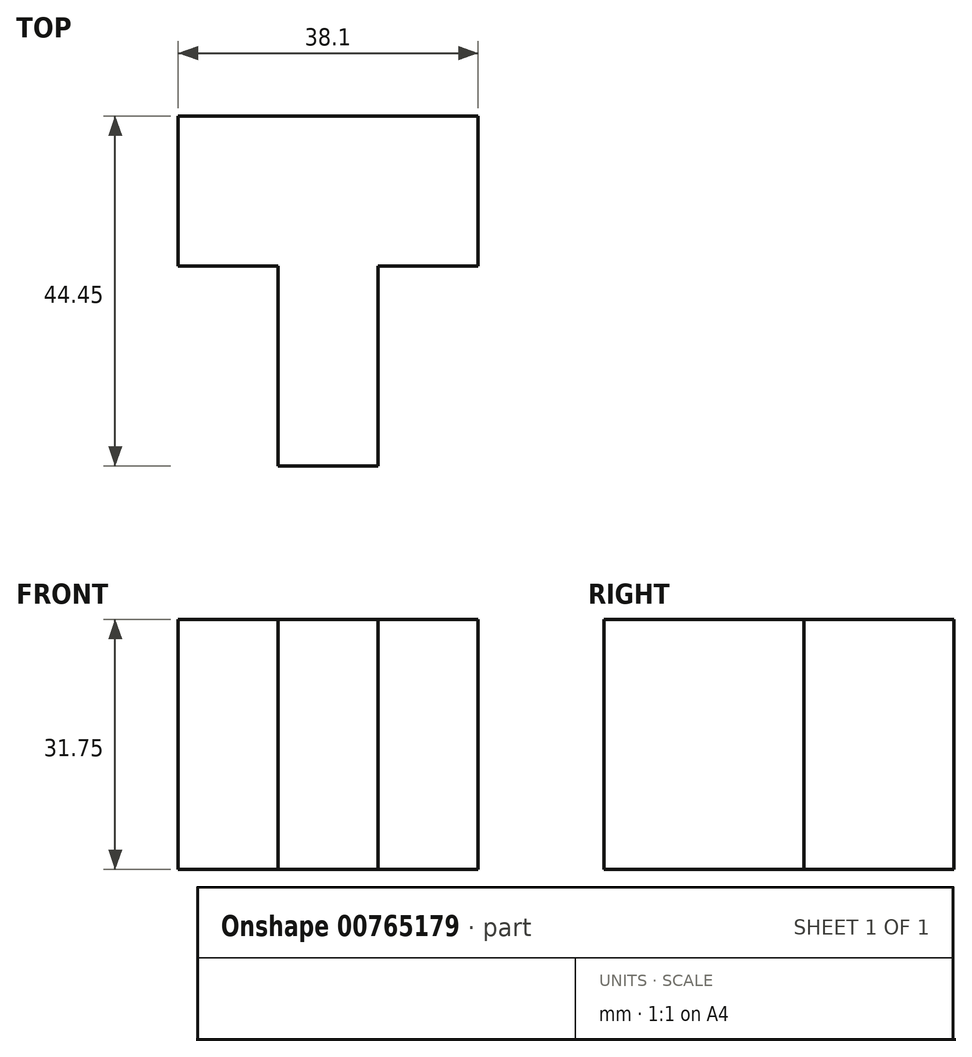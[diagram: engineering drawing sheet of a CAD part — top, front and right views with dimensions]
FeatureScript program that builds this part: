
annotation { "Feature Type Name" : "Feature", "Feature Type Description" : "" }
export const myFeature = defineFeature(function(context is Context, id is Id, definition is map)
    precondition{}
    {
        {
            var Q0;
            Q0=qCreatedBy(makeId("Top.planeOp"),FACE);
            var sketch = newSketch(context, id + "F0", { "sketchPlane" : qUnion([Q0])});
            skLineSegment(sketch, "E0", {"start": v(-25.4, 39.9) * mm, "end": v(12.7, 39.9) * mm});
            skLineSegment(sketch, "E1", {"start": v(-25.4, 39.9) * mm, "end": v(-25.4, 20.85) * mm});
            skLineSegment(sketch, "E2", {"start": v(12.7, 39.9) * mm, "end": v(12.7, 20.85) * mm});
            skLineSegment(sketch, "E3", {"start": v(-25.4, 20.85) * mm, "end": v(-12.7, 20.85) * mm});
            skLineSegment(sketch, "E4", {"start": v(12.7, 20.85) * mm, "end": v(0, 20.85) * mm});
            skLineSegment(sketch, "E5", {"start": v(-12.7, 20.85) * mm, "end": v(-12.7, -4.55) * mm});
            skLineSegment(sketch, "E6", {"start": v(0, 20.85) * mm, "end": v(0, -4.55) * mm});
            skLineSegment(sketch, "E7", {"start": v(-12.7, -4.55) * mm, "end": v(0, -4.55) * mm});
            skSolve(sketch);
        }
        {
            var Q0;
            Q0=makeQuery(id+"F0.imprint","IMPRINT",FACE,{"disambiguationData":[TD([[makeQuery(id+"F0.imprint","IMPRINT",EDGE,{"derivedFrom":sQuery(id+"F0.wireOp",EDGE,"E0")}),-1.0]])]});
            extrude(context, id + "F1", {"entities" : qUnion([Q0]), "depth" : 31.75 * mm, "offsetDistance" : 25.4 * mm});
        }
    });
